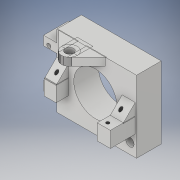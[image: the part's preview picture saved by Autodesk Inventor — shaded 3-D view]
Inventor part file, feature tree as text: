
AUTODESK INVENTOR PART (.ipt)
format: ipt  version: 2017 (Build 210142000, 142)  size: 1,157,120 bytes
history: native  units: in
note: dims shown in document units (in); Inventor stores cm internally (conversion verified against a paired STEP export)
features: projected_geometry x15, extrude x10, sketch x10, imported_body x1
ambient origin geometry x8: Origin, YZ Plane, XZ Plane, XY Plane, X Axis, Y Axis, Z Axis, Center Point
bodies: Solid1 (feature_tree)
feature tree (36):
  extrude  "Extrusion1"  Depth=0.3937in TaperAngle=0.0deg
  extrude  "Extrusion2"  Depth=0.3937in TaperAngle=0.0deg
  extrude  "Extrusion3"  Depth=1.839in
  extrude  "Extrusion4"  Depth=0.327in
  extrude  "Extrusion5"  Depth=0.125in
  extrude  "Extrusion6"  Depth=0.125in
  extrude  "Extrusion7"  Depth=0.5in TaperAngle=0.0deg
  extrude  "Extrusion8"  Depth=0.1562in TaperAngle=0.0deg
  extrude  "Extrusion9"  Depth=0.125in TaperAngle=0.0deg
  extrude  "Extrusion10"  Depth=0.6102in
  sketch  "Sketch1"  dims[d0=0.252in d1=0.3937in d2=0.0in]
  projected_geometry  "Projected Loop1"
  projected_geometry  "Projected Loop2"
  sketch  "Sketch2"  dims[d3=0.3937in d4=0.0in d5=0.625in d6=0.0in]
  projected_geometry  "Projected Loop3"
  sketch  "Sketch3"  dims[d7=0.197in d8=1.839in]
  projected_geometry  "Projected Loop4"
  sketch  "Sketch4"  dims[d9=1.709in d10=0.327in]
  projected_geometry  "Projected Loop5"
  sketch  "Sketch5"  dims[d11=0.125in d12=0.125in]
  projected_geometry  "Projected Loop6"
  sketch  "Sketch6"  dims[d13=0.125in d14=0.0in d15=0.25in]
  projected_geometry  "Projected Loop7"
  sketch  "Sketch7"  dims[d16=0.25in d17=0.5in d18=0.0in]
  projected_geometry  "Projected Loop8"
  sketch  "Sketch9"  dims[d19=0.25in d20=0.1562in d21=0.5in d22=0.0in d23=0.0in]
  projected_geometry  "Projected Loop10"
  projected_geometry  "Projected Loop11"
  projected_geometry  "Projected Loop12"
  projected_geometry  "Projected Loop13"
  projected_geometry  "Projected Loop14"
  sketch  "Sketch10"  dims[d24=1.2992in d25=0.125in d26=0.0in]
  projected_geometry  "Projected Loop15"
  sketch  "Sketch11"  dims[d27=0.0787in d28=0.0in d29=0.6102in d30=0.4528in d31=90.0deg d32=0.2756in d33=0.2756in d34=0.3937in d35=0.0in d39=0.1969in d40=0.0in d44=0.1575in d45=0.1939in d46=0.125in d47=0.1939in d48=0.125in d49=0.1575in]
  projected_geometry  "Projected Loop16"
  imported_body  "Base1"
